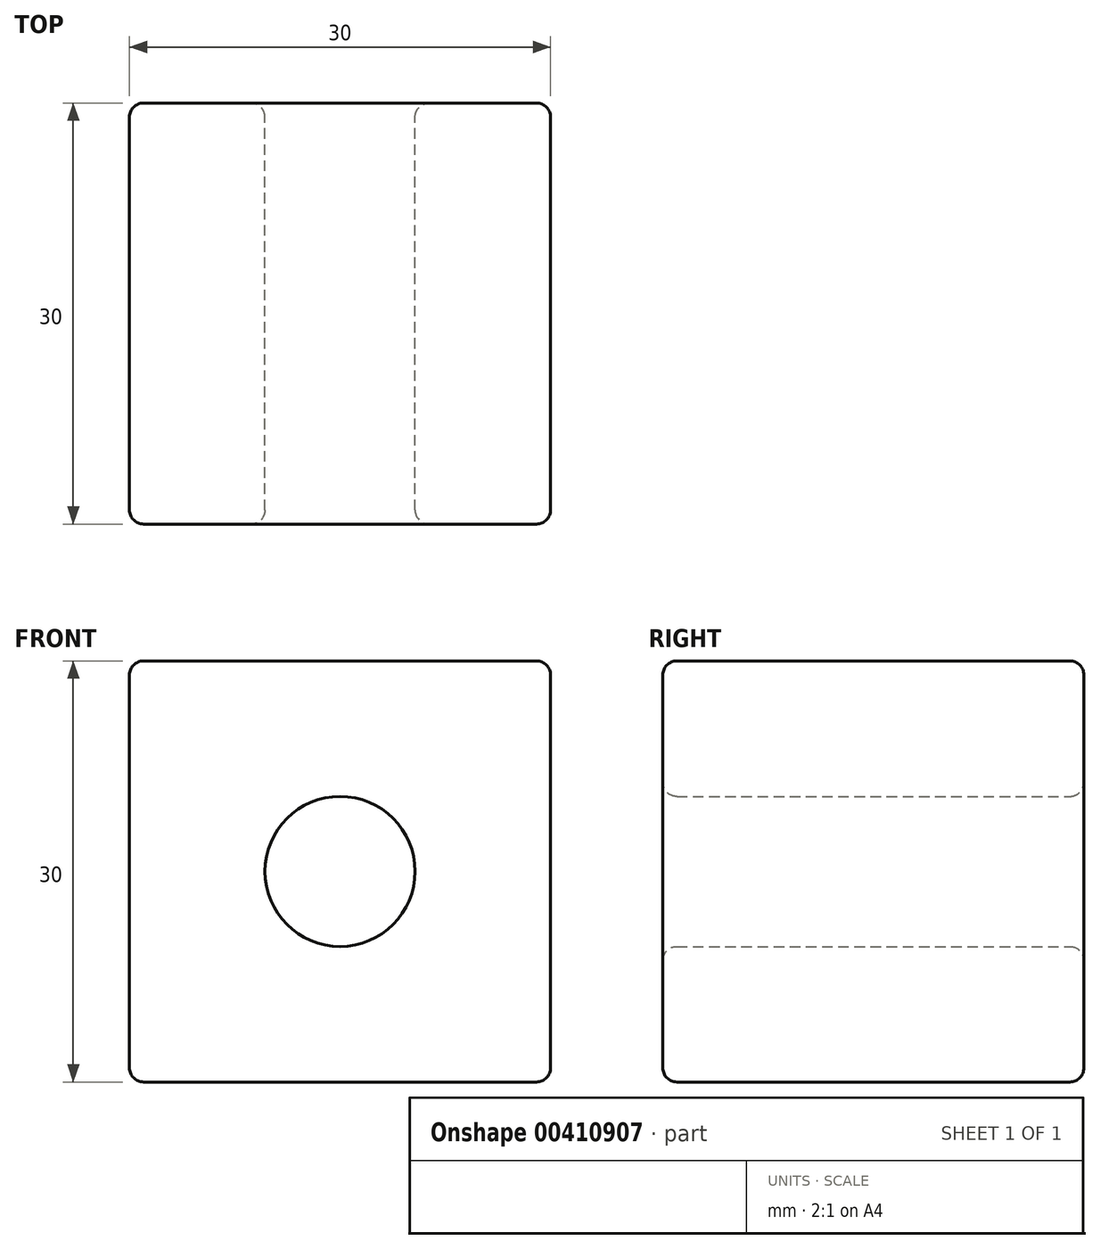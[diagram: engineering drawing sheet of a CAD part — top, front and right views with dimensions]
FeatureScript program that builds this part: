
annotation { "Feature Type Name" : "Feature", "Feature Type Description" : "" }
export const myFeature = defineFeature(function(context is Context, id is Id, definition is map)
    precondition{}
    {
        {
            var Q0;
            Q0=qCreatedBy(makeId("Front.planeOp"),FACE);
            var sketch = newSketch(context, id + "F0", { "sketchPlane" : qUnion([Q0])});
            skLineSegment(sketch, "E0.bottom", {"start": v(-30, 30) * mm, "end": v(0, 30) * mm});
            skLineSegment(sketch, "E0.top", {"start": v(-30, 0) * mm, "end": v(0, 0) * mm});
            skLineSegment(sketch, "E0.left", {"start": v(-30, 30) * mm, "end": v(-30, 0) * mm});
            skLineSegment(sketch, "E0.right", {"start": v(0, 30) * mm, "end": v(0, 0) * mm});
            skCircle(sketch, "E1", {"center": v(-15, 15) * mm, "radius": 5.35 * mm});
            skSolve(sketch);
        }
        {
            var Q0;
            Q0 = qSketchRegion(id + "F0", true);
            extrude(context, id + "F1", {"entities" : qUnion([Q0]), "depth" : 30 * mm});
        }
        {
            var Q0;
            Q0=makeQuery(id+"F1.opExtrude","CAP_EDGE",EDGE,{"disambiguationData":[OSD([sQuery(id+"F0.wireOp",EDGE,"E1")])],"isStart":false});
            var Q1;
            Q1=makeQuery(id+"F1.opExtrude","CAP_EDGE",EDGE,{"disambiguationData":[OSD([sQuery(id+"F0.wireOp",EDGE,"E0.bottom")])],"isStart":false});
            var Q2;
            Q2=makeQuery(id+"F1.opExtrude","CAP_FACE",FACE,{"disambiguationData":[OSD([sQuery(id+"F0.wireOp",EDGE,"E0.bottom"),sQuery(id+"F0.wireOp",EDGE,"E0.top"),sQuery(id+"F0.wireOp",EDGE,"E0.left"),sQuery(id+"F0.wireOp",EDGE,"E0.right"),sQuery(id+"F0.wireOp",EDGE,"E1")])],"isStart":false});
            var Q3;
            Q3=makeQuery(id+"F1.opExtrude","CAP_FACE",FACE,{"disambiguationData":[OSD([sQuery(id+"F0.wireOp",EDGE,"E0.bottom"),sQuery(id+"F0.wireOp",EDGE,"E0.top"),sQuery(id+"F0.wireOp",EDGE,"E0.left"),sQuery(id+"F0.wireOp",EDGE,"E0.right"),sQuery(id+"F0.wireOp",EDGE,"E1")])],"isStart":true});
            var Q4;
            Q4=makeQuery(id+"F1.opExtrude","SWEPT_FACE",FACE,{"disambiguationData":[OSD([sQuery(id+"F0.wireOp",EDGE,"E0.top")])]});
            var Q5;
            Q5=makeQuery(id+"F1.opExtrude","SWEPT_EDGE",EDGE,{"disambiguationData":[OSD([sQuery(id+"F0.wireOp",EDGE,"E0.bottom"),sQuery(id+"F0.wireOp",EDGE,"E0.left")])]});
            var Q6;
            Q6=makeQuery(id+"F1.opExtrude","SWEPT_EDGE",EDGE,{"disambiguationData":[OSD([sQuery(id+"F0.wireOp",EDGE,"E0.top"),sQuery(id+"F0.wireOp",EDGE,"E0.right")])]});
            var Q7;
            Q7=makeQuery(id+"F1.opExtrude","SWEPT_EDGE",EDGE,{"disambiguationData":[OSD([sQuery(id+"F0.wireOp",EDGE,"E0.bottom"),sQuery(id+"F0.wireOp",EDGE,"E0.right")])]});
            var Q8;
            Q8=makeQuery(id+"F1.opExtrude","CAP_EDGE",EDGE,{"disambiguationData":[OSD([sQuery(id+"F0.wireOp",EDGE,"E0.top")])],"isStart":false});
            var Q9;
            Q9=makeQuery(id+"F1.opExtrude","SWEPT_FACE",FACE,{"disambiguationData":[OSD([sQuery(id+"F0.wireOp",EDGE,"E0.left")])]});
            var Q10;
            Q10=makeQuery(id+"F1.opExtrude","SWEPT_FACE",FACE,{"disambiguationData":[OSD([sQuery(id+"F0.wireOp",EDGE,"E1")])]});
            var Q11;
            Q11=makeQuery(id+"F1.opExtrude","SWEPT_FACE",FACE,{"disambiguationData":[OSD([sQuery(id+"F0.wireOp",EDGE,"E0.right")])]});
            var Q12;
            Q12=makeQuery(id+"F1.opExtrude","CAP_EDGE",EDGE,{"disambiguationData":[OSD([sQuery(id+"F0.wireOp",EDGE,"E0.bottom")])],"isStart":true});
            var Q13;
            Q13=makeQuery(id+"F1.opExtrude","SWEPT_FACE",FACE,{"disambiguationData":[OSD([sQuery(id+"F0.wireOp",EDGE,"E0.bottom")])]});
            var Q14;
            Q14=makeQuery(id+"F1.opExtrude","SWEPT_EDGE",EDGE,{"disambiguationData":[OSD([sQuery(id+"F0.wireOp",EDGE,"E0.top"),sQuery(id+"F0.wireOp",EDGE,"E0.left")])]});
            var Q15;
            Q15=makeQuery(id+"F1.opExtrude","CAP_EDGE",EDGE,{"disambiguationData":[OSD([sQuery(id+"F0.wireOp",EDGE,"E1")])],"isStart":true});
            var Q16;
            Q16=makeQuery(id+"F1.opExtrude","CAP_EDGE",EDGE,{"disambiguationData":[OSD([sQuery(id+"F0.wireOp",EDGE,"E0.right")])],"isStart":false});
            var Q17;
            Q17=makeQuery(id+"F1.opExtrude","CAP_EDGE",EDGE,{"disambiguationData":[OSD([sQuery(id+"F0.wireOp",EDGE,"E0.right")])],"isStart":true});
            var Q18;
            Q18=makeQuery(id+"F1.opExtrude","CAP_EDGE",EDGE,{"disambiguationData":[OSD([sQuery(id+"F0.wireOp",EDGE,"E0.left")])],"isStart":false});
            var Q19;
            Q19=makeQuery(id+"F1.opExtrude","CAP_EDGE",EDGE,{"disambiguationData":[OSD([sQuery(id+"F0.wireOp",EDGE,"E0.left")])],"isStart":true});
            var Q20;
            Q20=makeQuery(id+"F1.opExtrude","CAP_EDGE",EDGE,{"disambiguationData":[OSD([sQuery(id+"F0.wireOp",EDGE,"E0.top")])],"isStart":true});
            fillet(context, id + "F2", {"entities" : qUnion([Q0, Q1, Q2, Q3, Q4, Q5, Q6, Q7, Q8, Q9, Q10, Q11, Q12, Q13, Q14, Q15, Q16, Q17, Q18, Q19, Q20]), "radius" : 1 * mm, "tangentPropagation" : true, "allowEdgeOverflow" : false});
        }
    });
